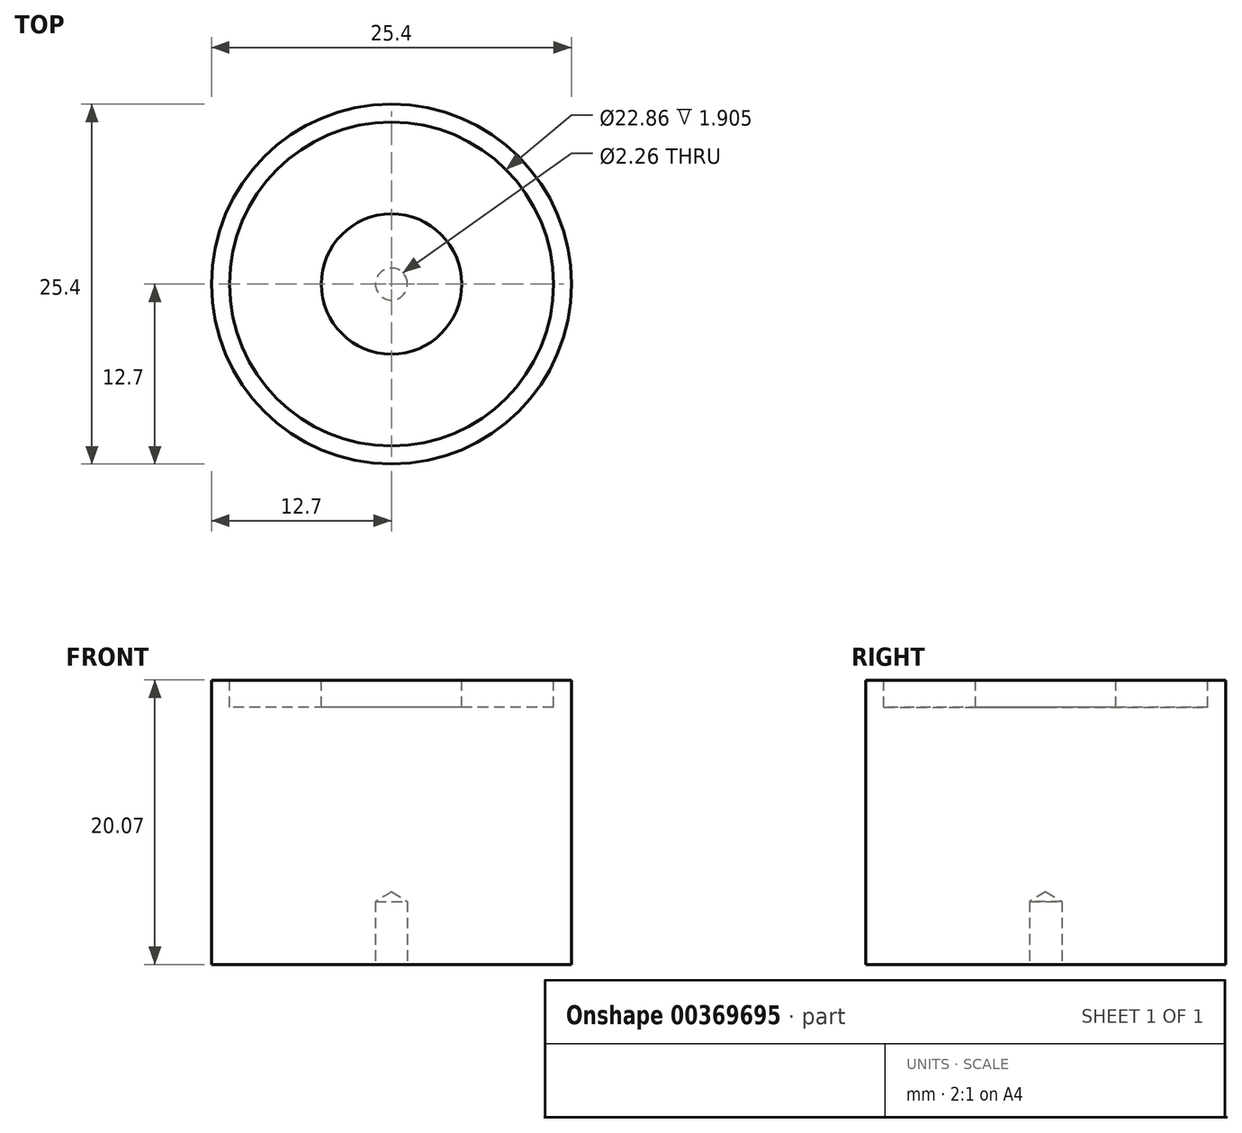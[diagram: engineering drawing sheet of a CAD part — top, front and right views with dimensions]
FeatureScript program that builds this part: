
annotation { "Feature Type Name" : "Feature", "Feature Type Description" : "" }
export const myFeature = defineFeature(function(context is Context, id is Id, definition is map)
    precondition{}
    {
        {
            var Q0;
            Q0=qCreatedBy(makeId("Top.planeOp"),FACE);
            var sketch = newSketch(context, id + "F0", { "sketchPlane" : qUnion([Q0])});
            skCircle(sketch, "E0", {"center": v(0, 0) * mm, "radius": 12.7 * mm});
            skSolve(sketch);
        }
        {
            var Q0;
            Q0=qSketchRegion(id+"F0",true);
            extrude(context, id + "F1", {"entities" : qUnion([Q0]), "depth" : 20.07 * mm});
        }
        {
            var Q0;
            Q0=makeQuery(id+"F1.opExtrude","CAP_FACE",FACE,{"disambiguationData":[OSD([sQuery(id+"F0.wireOp",EDGE,"E0")])],"isStart":false});
            var sketch = newSketch(context, id + "F2", { "sketchPlane" : qUnion([Q0])});
            skCircle(sketch, "E1", {"center": v(0, 0) * mm, "radius": 11.43 * mm});
            skCircle(sketch, "E2", {"center": v(0, 0) * mm, "radius": 4.95 * mm});
            skSolve(sketch);
        }
        {
            var Q0;
            Q0=qSketchRegion(id+"F2",true);
            extrude(context, id + "F3", {"entities" : qUnion([Q0]), "operationType" : NewBodyOperationType.REMOVE, "oppositeDirection" : true, "depth" : 1.9 * mm});
        }
        {
            var Q0;
            Q0=makeQuery(id+"F1.opExtrude","CAP_FACE",FACE,{"disambiguationData":[OSD([sQuery(id+"F0.wireOp",EDGE,"E0")])],"isStart":true});
            var sketch = newSketch(context, id + "F4", { "sketchPlane" : qUnion([Q0])});
            skPoint(sketch, "E3", {"position": v(0, 0) * mm});
            skSolve(sketch);
        }
        {
            var Q0;
            Q0=sQuery(id+"F4.wireOp",VERTEX,"E3");
            var Q1;
            Q1=makeQuery(id+"F1.opExtrude","SWEPT_BODY",BODY,{"disambiguationData":[OSD([sQuery(id+"F0.wireOp",EDGE,"E0")])]});
            hole(context, id + "F5", {"style" : HoleStyle.SIMPLE, "endStyle" : HoleEndStyle.BLIND, "standardTappedOrClearance" : lookupTablePath({ "standard" : "ANSI", "engagement" : "75%", "pitch" : "40 tpi", "size" : "#4", "type" : "Tapped" }), "standardBlindInLast" : lookupTablePath({ "standard" : "ANSI", "engagement" : "75%", "pitch" : "40 tpi", "size" : "#4", "type" : "Tapped" }), "holeDiameter" : 2.26 * mm, "showTappedDepth" : true, "holeDepth" : 4.45 * mm, "tappedDepth" : 2.54 * mm, "tapClearance" : 3, "locations" : qUnion([Q0]), "scope" : qUnion([Q1]), "majorDiameter" : 2.84 * mm});
        }
    });
